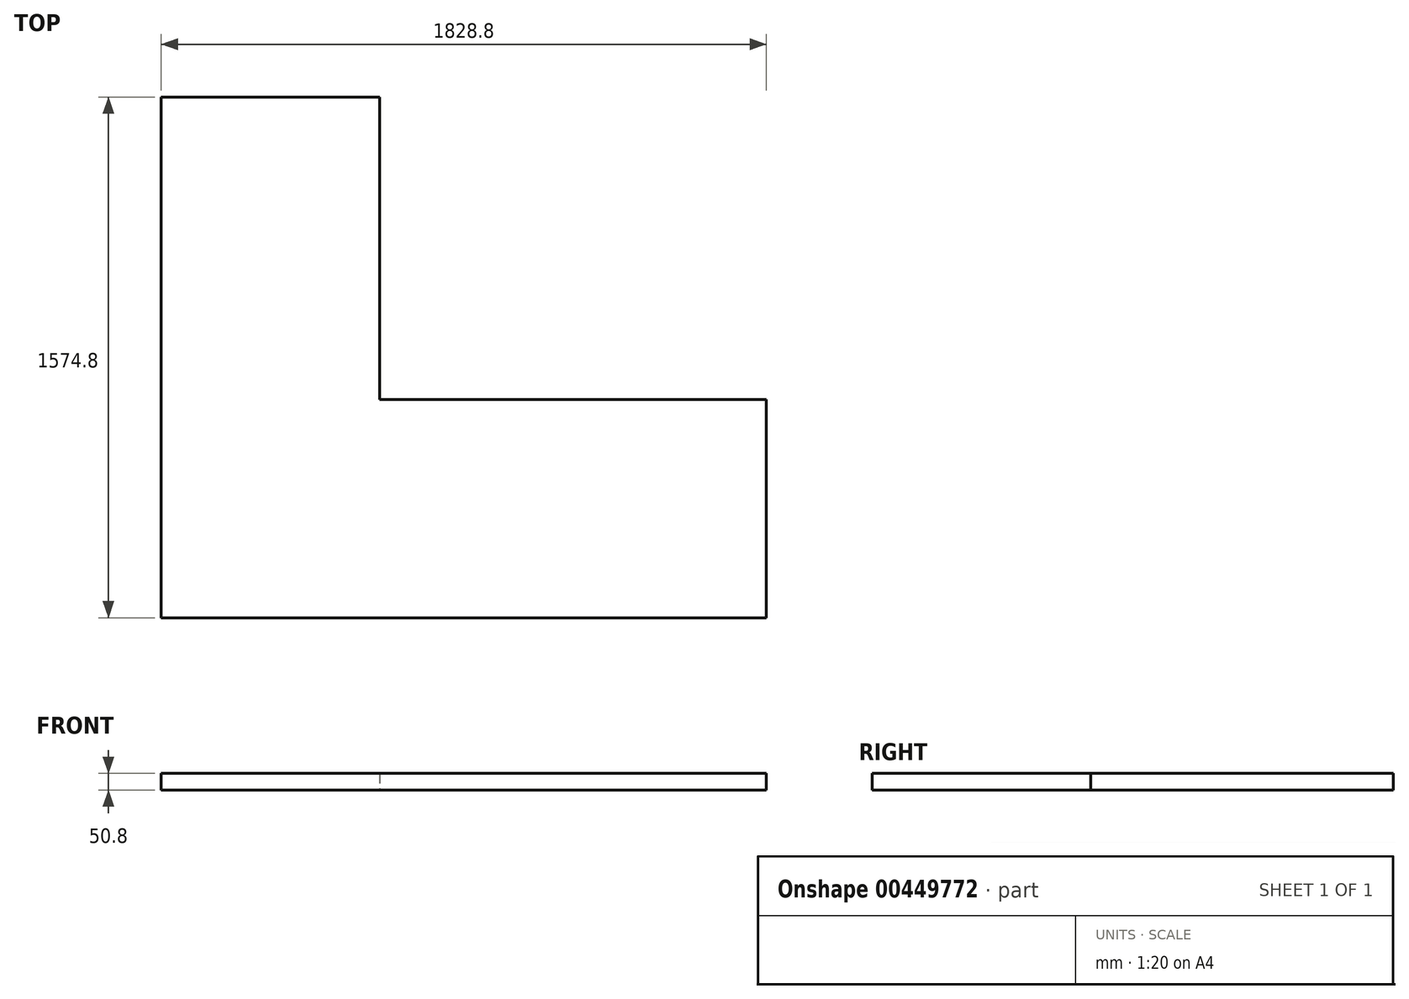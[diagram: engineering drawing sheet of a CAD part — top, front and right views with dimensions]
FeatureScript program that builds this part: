
annotation { "Feature Type Name" : "Feature", "Feature Type Description" : "" }
export const myFeature = defineFeature(function(context is Context, id is Id, definition is map)
    precondition{}
    {
        {
            var Q0;
            Q0=qCreatedBy(makeId("Top.planeOp"),FACE);
            var sketch = newSketch(context, id + "F0", { "sketchPlane" : qUnion([Q0])});
            skLineSegment(sketch, "E0", {"start": v(-919.72, -31.33) * mm, "end": v(909.08, -31.33) * mm});
            skLineSegment(sketch, "E1", {"start": v(909.08, -31.33) * mm, "end": v(909.08, 629.07) * mm});
            skLineSegment(sketch, "E2", {"start": v(-919.72, -31.33) * mm, "end": v(-919.72, 1543.47) * mm});
            skLineSegment(sketch, "E3", {"start": v(-919.72, 1543.47) * mm, "end": v(-259.32, 1543.47) * mm});
            skLineSegment(sketch, "E4", {"start": v(-259.32, 1543.47) * mm, "end": v(-259.32, 629.07) * mm});
            skLineSegment(sketch, "E5", {"start": v(-259.32, 629.07) * mm, "end": v(909.08, 629.07) * mm});
            skSolve(sketch);
        }
        {
            var Q0;
            Q0=makeQuery(id+"F0.imprint","IMPRINT",FACE,{"disambiguationData":[TD([[makeQuery(id+"F0.imprint","IMPRINT",EDGE,{"derivedFrom":sQuery(id+"F0.wireOp",EDGE,"E0")}),1.0]])]});
            extrude(context, id + "F1", {"entities" : qUnion([Q0]), "depth" : 50.8 * mm});
        }
    });
